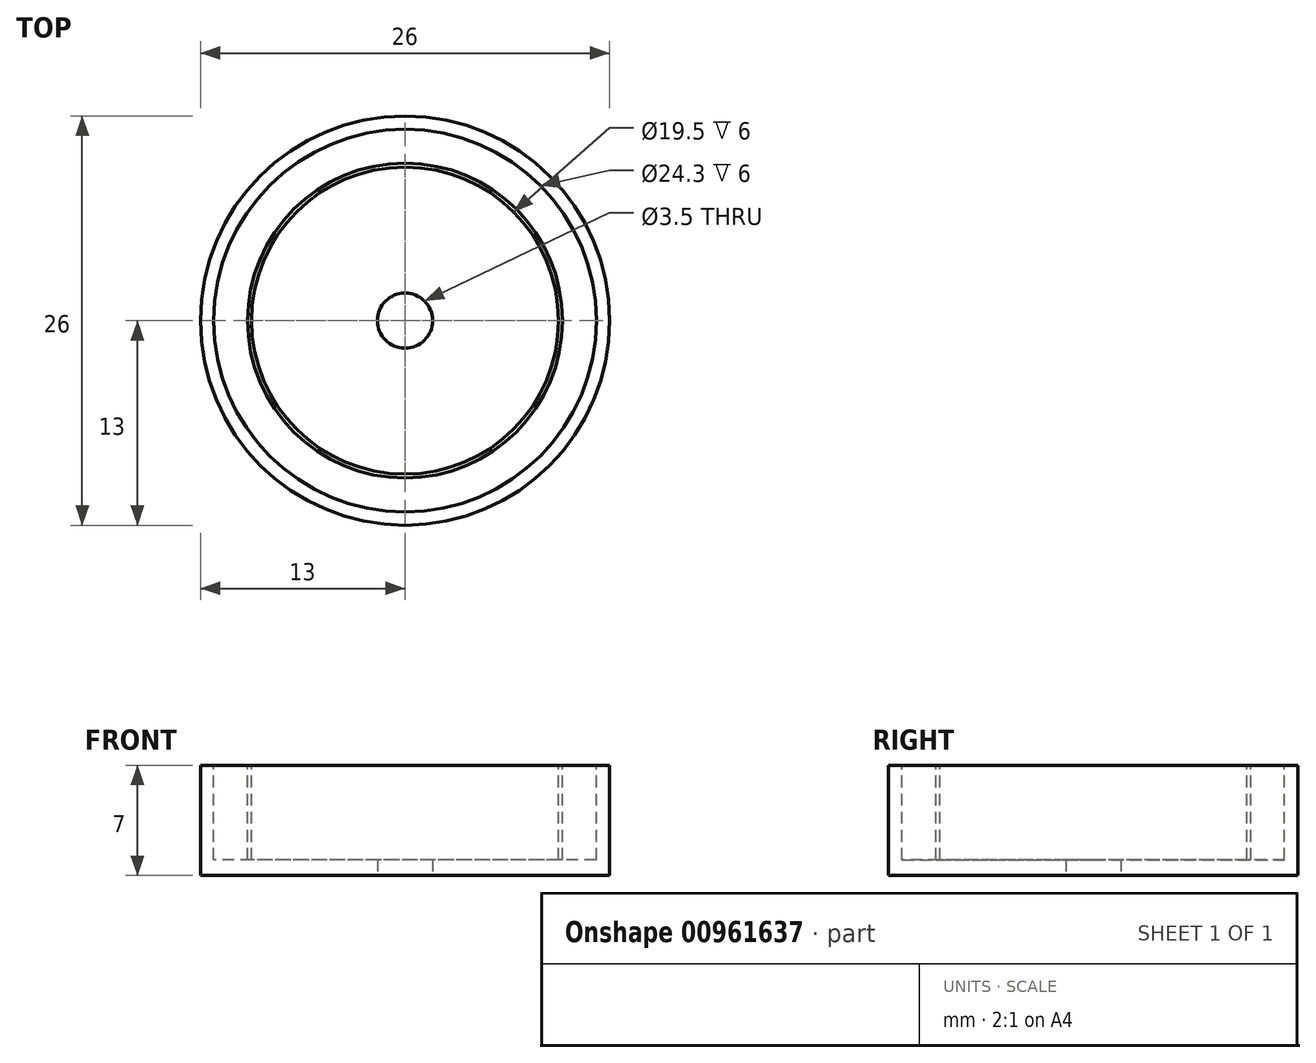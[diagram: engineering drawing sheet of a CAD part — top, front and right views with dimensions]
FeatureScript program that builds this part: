
annotation { "Feature Type Name" : "Feature", "Feature Type Description" : "" }
export const myFeature = defineFeature(function(context is Context, id is Id, definition is map)
    precondition{}
    {
        {
            var Q0;
            Q0=qCreatedBy(makeId("Top.planeOp"),FACE);
            var sketch = newSketch(context, id + "F0", { "sketchPlane" : qUnion([Q0])});
            skCircle(sketch, "E0", {"center": v(0, 0) * mm, "radius": 13 * mm});
            skSolve(sketch);
        }
        {
            var Q0;
            Q0=makeQuery(id+"F0.imprint","IMPRINT",FACE,{"disambiguationData":[TD([[makeQuery(id+"F0.imprint","IMPRINT",EDGE,{"derivedFrom":sQuery(id+"F0.wireOp",EDGE,"E0")}),1.0]])]});
            extrude(context, id + "F1", {"entities" : qUnion([Q0]), "depth" : 7 * mm, "offsetDistance" : 25 * mm});
        }
        {
            var Q0;
            Q0=makeQuery(id+"F1.opExtrude","CAP_FACE",FACE,{"disambiguationData":[OSD([sQuery(id+"F0.wireOp",EDGE,"E0")])],"isStart":false});
            var sketch = newSketch(context, id + "F2", { "sketchPlane" : qUnion([Q0])});
            skCircle(sketch, "E1", {"center": v(0, 0) * mm, "radius": 9.75 * mm});
            skSolve(sketch);
        }
        {
            var Q0;
            Q0=makeQuery(id+"F2.imprint","IMPRINT",FACE,{"disambiguationData":[TD([[makeQuery(id+"F2.imprint","IMPRINT",EDGE,{"derivedFrom":sQuery(id+"F2.wireOp",EDGE,"E1")}),1.0]])]});
            extrude(context, id + "F3", {"entities" : qUnion([Q0]), "operationType" : NewBodyOperationType.REMOVE, "oppositeDirection" : true, "depth" : 6 * mm, "offsetDistance" : 25 * mm});
        }
        {
            var Q0;
            Q0=makeQuery(id+"F1.opExtrude","CAP_FACE",FACE,{"disambiguationData":[OSD([sQuery(id+"F0.wireOp",EDGE,"E0")])],"isStart":false});
            var sketch = newSketch(context, id + "F4", { "sketchPlane" : qUnion([Q0])});
            skCircle(sketch, "E2", {"center": v(0, 0) * mm, "radius": 12.15 * mm});
            skSolve(sketch);
        }
        {
            var Q0;
            Q0=makeQuery(id+"F4.imprint","IMPRINT",FACE,{"disambiguationData":[TD([[makeQuery(id+"F4.imprint","IMPRINT",EDGE,{"derivedFrom":sQuery(id+"F4.wireOp",EDGE,"E2")}),1.0]])]});
            var sketch = newSketch(context, id + "F5", { "sketchPlane" : qUnion([Q0])});
            skCircle(sketch, "E3", {"center": v(0, 0) * mm, "radius": 10 * mm});
            skCircle(sketch, "E4", {"center": v(0, 0) * mm, "radius": 12.5 * mm});
            skSolve(sketch);
        }
        {
            var Q0;
            Q0=makeQuery(id+"F5.imprint","IMPRINT",FACE,{"disambiguationData":[TD([[makeQuery(id+"F5.imprint","IMPRINT",EDGE,{"derivedFrom":sQuery(id+"F5.wireOp",EDGE,"E3")}),-1.0]])]});
            extrude(context, id + "F6", {"entities" : qUnion([Q0]), "operationType" : NewBodyOperationType.REMOVE, "oppositeDirection" : true, "depth" : 6 * mm, "offsetDistance" : 25 * mm});
        }
        {
            var Q0;
            Q0=makeQuery(id+"F1.opExtrude","CAP_FACE",FACE,{"disambiguationData":[OSD([sQuery(id+"F0.wireOp",EDGE,"E0")])],"isStart":true});
            var sketch = newSketch(context, id + "F7", { "sketchPlane" : qUnion([Q0])});
            skCircle(sketch, "E5", {"center": v(0, 0) * mm, "radius": 1.75 * mm});
            skSolve(sketch);
        }
        {
            var Q0;
            Q0=makeQuery(id+"F7.imprint","IMPRINT",FACE,{"disambiguationData":[TD([[makeQuery(id+"F7.imprint","IMPRINT",EDGE,{"derivedFrom":sQuery(id+"F7.wireOp",EDGE,"E5")}),1.0]])]});
            extrude(context, id + "F8", {"entities" : qUnion([Q0]), "operationType" : NewBodyOperationType.REMOVE, "oppositeDirection" : true, "depth" : 25 * mm, "offsetDistance" : 25 * mm});
        }
    });
